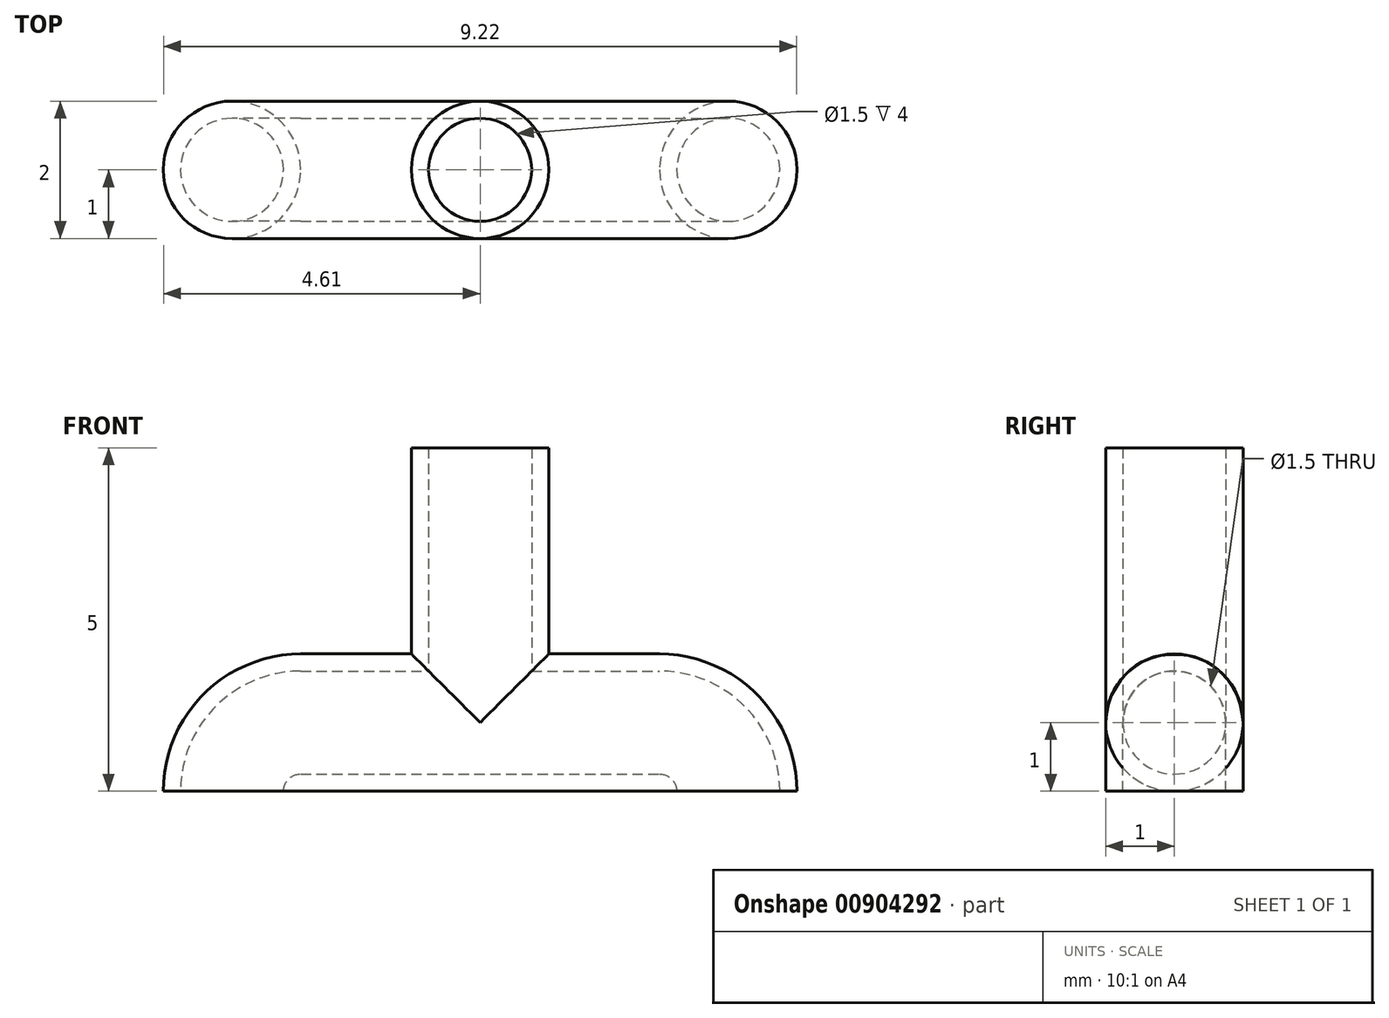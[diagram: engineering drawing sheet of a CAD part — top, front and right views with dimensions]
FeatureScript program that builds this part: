
annotation { "Feature Type Name" : "Feature", "Feature Type Description" : "" }
export const myFeature = defineFeature(function(context is Context, id is Id, definition is map)
    precondition{}
    {
        {
            var Q0;
            Q0=qCreatedBy(makeId("Top.planeOp"),FACE);
            var sketch = newSketch(context, id + "F0", { "sketchPlane" : qUnion([Q0])});
            skLineSegment(sketch, "E0.bottom", {"start": v(3.61, 0) * mm, "end": v(-3.61, 0) * mm});
            skLineSegment(sketch, "E0.top", {"start": v(3.61, 0) * mm, "end": v(-3.61, 0) * mm});
            skLineSegment(sketch, "E0.left", {"start": v(3.61, 0) * mm, "end": v(3.61, 0) * mm});
            skLineSegment(sketch, "E0.right", {"start": v(-3.61, 0) * mm, "end": v(-3.61, 0) * mm});
            skPoint(sketch, "E0.middle", {"position": v(0, 0) * mm});
            skCircle(sketch, "E1", {"center": v(-3.61, 0) * mm, "radius": 0.75 * mm});
            skCircle(sketch, "E2", {"center": v(-3.61, 0) * mm, "radius": 1 * mm});
            skCircle(sketch, "E3", {"center": v(3.61, 0) * mm, "radius": 0.75 * mm});
            skCircle(sketch, "E4", {"center": v(3.61, 0) * mm, "radius": 1 * mm});
            skSolve(sketch);
        }
        {
            var Q0;
            Q0=qCreatedBy(makeId("Front.planeOp"),FACE);
            var sketch = newSketch(context, id + "F1", { "sketchPlane" : qUnion([Q0])});
            skLineSegment(sketch, "E5.0", {"start": v(-4.61, 0) * mm, "end": v(-2.61, 0) * mm});
            skLineSegment(sketch, "E6.0", {"start": v(2.61, 0) * mm, "end": v(4.61, 0) * mm});
            skLineSegment(sketch, "E7", {"start": v(-2.61, 0) * mm, "end": v(-2.61, 2) * mm});
            skLineSegment(sketch, "E8", {"start": v(-2.61, 1) * mm, "end": v(-1.94, 1) * mm});
            skArc(sketch, "E9", {"start": v(-2.61, 1) * mm, "mid": v(-3.32, 0.7) * mm, "end": v(-3.61, 0) * mm});
            skLineSegment(sketch, "E10", {"start": v(0, 0) * mm, "end": v(0, 0.78) * mm});
            skLineSegment(sketch, "E11.MirrorCS", {"start": v(2.61, 0) * mm, "end": v(2.61, 2) * mm});
            skArc(sketch, "E12.MirrorCS", {"start": v(2.61, 1) * mm, "mid": v(3.32, 0.7) * mm, "end": v(3.61, 0) * mm});
            skSolve(sketch);
        }
        {
            var Q0;
            Q0=makeQuery(id+"F0.imprint","IMPRINT",FACE,{"disambiguationData":[TD([[makeQuery(id+"F0.imprint","IMPRINT",EDGE,{"derivedFrom":sQuery(id+"F0.wireOp",EDGE,"E1")}),-1.0]])]});
            var Q1;
            Q1=sQuery(id+"F1.wireOp",EDGE,"E9");
            sweep(context, id + "F2", {"profiles" : qUnion([Q0]), "path" : qUnion([Q1])});
        }
        {
            var Q0;
            Q0=makeQuery(id+"F0.imprint","IMPRINT",FACE,{"disambiguationData":[TD([[makeQuery(id+"F0.imprint","IMPRINT",EDGE,{"derivedFrom":sQuery(id+"F0.wireOp",EDGE,"E3")}),-1.0]])]});
            var Q1;
            Q1=sQuery(id+"F1.wireOp",EDGE,"E12.MirrorCS");
            sweep(context, id + "F3", {"profiles" : qUnion([Q0]), "path" : qUnion([Q1])});
        }
        {
            var Q0;
            Q0=makeQuery(id+"F3.opSweep","CAP_FACE",FACE,{"disambiguationData":[OSD([sQuery(id+"F0.wireOp",EDGE,"E3"),sQuery(id+"F0.wireOp",EDGE,"E4"),sQuery(id+"F1.wireOp",VERTEX,"E12.MirrorCS.start")])],"isStart":false});
            extrude(context, id + "F4", {"entities" : qUnion([Q0]), "operationType" : NewBodyOperationType.ADD, "depth" : 2.6 * mm, "offsetDistance" : 25 * mm});
        }
        {
            var Q0;
            Q0=makeQuery(id+"F2.opSweep","CAP_FACE",FACE,{"disambiguationData":[OSD([sQuery(id+"F0.wireOp",EDGE,"E1"),sQuery(id+"F0.wireOp",EDGE,"E2"),sQuery(id+"F1.wireOp",VERTEX,"E9.start")])],"isStart":false});
            extrude(context, id + "F5", {"entities" : qUnion([Q0]), "depth" : 2.6 * mm, "offsetDistance" : 25 * mm});
        }
        {
            var Q0;
            Q0=makeQuery(id+"F2.opSweep","SWEPT_BODY",BODY,{"disambiguationData":[OSD([sQuery(id+"F0.wireOp",EDGE,"E1"),sQuery(id+"F0.wireOp",EDGE,"E2"),sQuery(id+"F1.wireOp",EDGE,"E9")])]});
            var Q1;
            Q1=makeQuery(id+"F3.opSweep","SWEPT_BODY",BODY,{"disambiguationData":[OSD([sQuery(id+"F0.wireOp",EDGE,"E3"),sQuery(id+"F0.wireOp",EDGE,"E4"),sQuery(id+"F1.wireOp",EDGE,"E12.MirrorCS")])]});
            var Q2;
            Q2=makeQuery(id+"F5.opExtrude","SWEPT_BODY",BODY,{"disambiguationData":[OSD([sQuery(id+"F0.wireOp",EDGE,"E1"),sQuery(id+"F0.wireOp",EDGE,"E2"),sQuery(id+"F1.wireOp",VERTEX,"E9.start")])]});
            booleanBodies(context, id + "F6", {"operationType" : BooleanOperationType.UNION, "tools" : qUnion([Q0, Q1, Q2])});
        }
        {
            var Q0;
            Q0=qCreatedBy(makeId("Top.planeOp"),FACE);
            cPlane(context, id + "F7", {"entities" : qUnion([Q0]), "cplaneType" : CPlaneType.OFFSET, "offset" : 1 * mm, "width" : 150 * mm, "height" : 150 * mm});
        }
        {
            var Q0;
            Q0=qCreatedBy(id+"F7.planeOp",FACE);
            var sketch = newSketch(context, id + "F8", { "sketchPlane" : qUnion([Q0])});
            skCircle(sketch, "E13", {"center": v(0, 0) * mm, "radius": 1 * mm});
            skCircle(sketch, "E14", {"center": v(0, 0) * mm, "radius": 0.75 * mm});
            skSolve(sketch);
        }
        {
            var Q0;
            Q0=makeQuery(id+"F8.imprint","IMPRINT",FACE,{"disambiguationData":[TD([[makeQuery(id+"F8.imprint","IMPRINT",EDGE,{"derivedFrom":sQuery(id+"F8.wireOp",EDGE,"E13")}),1.0]])]});
            extrude(context, id + "F9", {"entities" : qUnion([Q0]), "operationType" : NewBodyOperationType.ADD, "depth" : 4 * mm, "offsetDistance" : 25 * mm});
        }
        {
            var Q0;
            Q0=makeQuery(id+"F9.opExtrude","CAP_FACE",FACE,{"disambiguationData":[OSD([sQuery(id+"F8.wireOp",EDGE,"E13"),sQuery(id+"F8.wireOp",EDGE,"E14")])],"isStart":false});
            var sketch = newSketch(context, id + "F10", { "sketchPlane" : qUnion([Q0])});
            skCircle(sketch, "E15.0", {"center": v(0, 0) * mm, "radius": 0.75 * mm});
            skSolve(sketch);
        }
        {
            var Q0;
            Q0=makeQuery(id+"F10.imprint","IMPRINT",FACE,{"disambiguationData":[TD([[makeQuery(id+"F10.imprint","IMPRINT",EDGE,{"derivedFrom":sQuery(id+"F10.wireOp",EDGE,"E15.0")}),1.0]])]});
            extrude(context, id + "F11", {"entities" : qUnion([Q0]), "operationType" : NewBodyOperationType.REMOVE, "oppositeDirection" : true, "depth" : 4 * mm, "offsetDistance" : 25 * mm});
        }
        {
            var Q0;
            Q0=qCreatedBy(makeId("Right.planeOp"),FACE);
            cPlane(context, id + "F12", {"entities" : qUnion([Q0]), "cplaneType" : CPlaneType.OFFSET, "offset" : 2 * mm, "width" : 150 * mm, "height" : 150 * mm});
        }
        {
            var Q0;
            Q0=qCreatedBy(id+"F12.planeOp",FACE);
            var sketch = newSketch(context, id + "F13", { "sketchPlane" : qUnion([Q0])});
            skCircle(sketch, "E16.0", {"center": v(0, 1) * mm, "radius": 1 * mm});
            skCircle(sketch, "E17", {"center": v(0, 1) * mm, "radius": 0.75 * mm});
            skSolve(sketch);
        }
        {
            var Q0;
            Q0=makeQuery(id+"F13.imprint","IMPRINT",FACE,{"disambiguationData":[TD([[makeQuery(id+"F13.imprint","IMPRINT",EDGE,{"derivedFrom":sQuery(id+"F13.wireOp",EDGE,"E17")}),1.0]])]});
            extrude(context, id + "F14", {"entities" : qUnion([Q0]), "operationType" : NewBodyOperationType.REMOVE, "oppositeDirection" : true, "depth" : 4 * mm, "offsetDistance" : 25 * mm});
        }
    });
